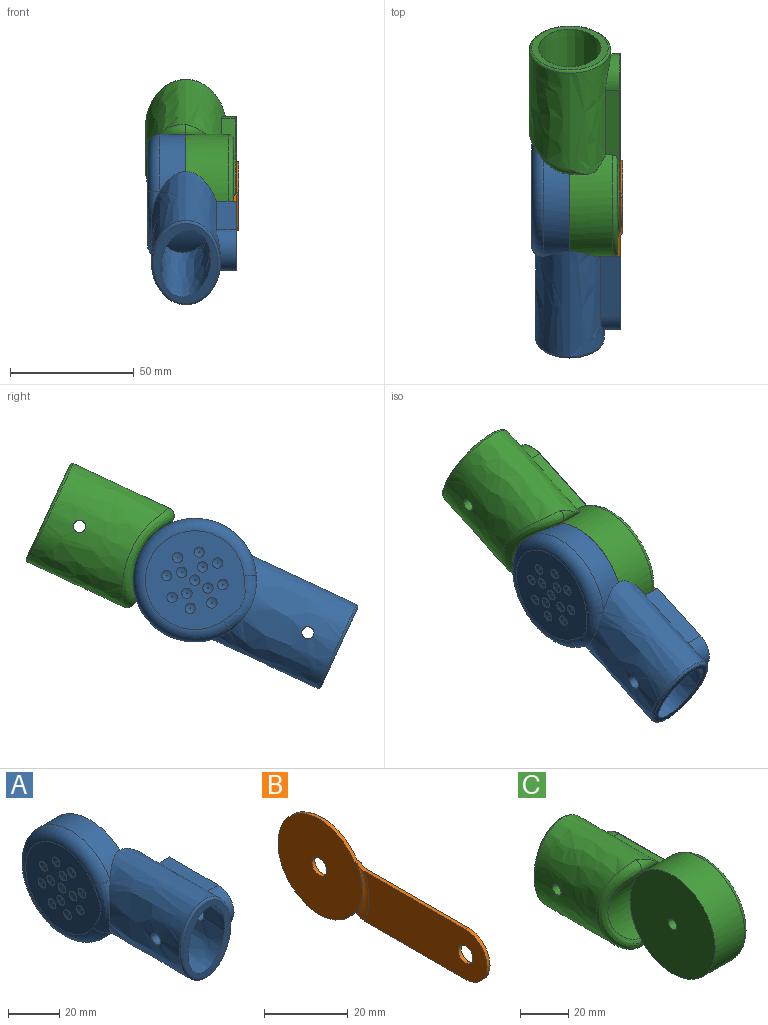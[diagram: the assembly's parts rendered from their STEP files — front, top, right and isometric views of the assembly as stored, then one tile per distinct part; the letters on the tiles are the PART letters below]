
ASSEMBLY  parts=3 mates=2
PART A: 53 faces, bbox 36x91.6x54.1 mm
  f0: cylinder r=2.5mm len=5mm, axis (1,0,0), area 58mm2, adj f1,f22
  f1: extruded ~46.96x37.5mm, area 3767.3mm2, adj f0,f2,f5,f7,f8,f9,f10,f11
  f2: cylinder r=25mm len=50mm, axis (1,0,0), area 1260.2mm2, adj f1,f4,f24
  f3: plane 41.43x40mm, normal (-1,0,0), area 1091.5mm2, adj f24,f25,f40,f41,f42,f43,f44,f45
  f4: plane 50x50mm, normal (1,0,0), area 1963.5mm2, adj f2,f5
  f5: cylinder r=25mm len=37.5mm, axis (1,0,0), area 450.2mm2, adj f1,f4
  f6: plane 35.51x26.01mm, normal (0,-1,0), area 252.8mm2, adj f22,f26
  f7: plane 26.98x8.07mm, normal (0,0,1), area 217.7mm2, adj f1,f8,f14,f15
  f8: cylinder r=8.75mm len=17.5mm, axis (1,0,0), area 199.2mm2, adj f1,f7,f9,f15
  f9: plane 26.96x8.07mm, normal (0,0,-1), area 217.5mm2, adj f1,f8,f10,f15
  f10: plane 8.07x1.26mm, normal (0,0.95,0.32), area 10.3mm2, adj f1,f9,f11,f15
  f11: plane 26.55x7.62mm, normal (0,0,1), area 202.3mm2, adj f1,f10,f12,f15
  f12: cylinder r=7.5mm len=15mm, axis (1,0,0), area 165.6mm2, adj f1,f11,f13,f15
  f13: plane 26.55x7.62mm, normal (0,0,-1), area 202.3mm2, adj f1,f12,f14,f15
  f14: plane 8.07x1.26mm, normal (0,0.94,-0.33), area 10.4mm2, adj f1,f7,f13,f15
  f15: plane 35.73x17.5mm, normal (1,0,0), area 98.8mm2, adj f7,f8,f9,f10,f11,f12,f13,f14
  f16: cylinder r=7.4mm len=14.8mm, axis (1,0,0), area 135.1mm2, adj f1,f17,f19,f20
  f17: plane 26.55x6.39mm, normal (0,0,-1), area 169.5mm2, adj f1,f16,f18,f20
  f18: extruded ~14.8x6.39mm, area 84.6mm2, adj f1,f17,f19,f20
  f19: plane 26.59x6.39mm, normal (0,0,1), area 169.8mm2, adj f1,f16,f18,f20
  f20: plane 33.99x14.8mm, normal (1,0,0), area 448.3mm2, adj f16,f17,f18,f19,f21
  f21: cylinder r=2.5mm len=9.55mm, axis (1,0,0), area 150mm2, adj f20,f22
  f22: extruded ~42.41x29.66mm, area 3105.8mm2, adj f0,f6,f21,f23
  f23: cylinder r=25mm len=29.75mm, axis (1,0,0), area 495.6mm2, adj f22
  f24: torus R=20mm, axis (1,0,0), area 955mm2, adj f2,f3,f25
  f25: bspline ~26.99x8.34mm, area 129mm2, adj f1,f3,f24
  f26: bspline ~37.52x28.01mm, area 158.9mm2, adj f1,f6
  f27: plane 0.28x0.28mm, normal (-1,0,0), area 0.1mm2, adj f52
  f28: plane 0.28x0.28mm, normal (-1,0,0), area 0.1mm2, adj f40
  f29: plane 0.28x0.28mm, normal (-1,0,0), area 0.1mm2, adj f41
  f30: plane 0.28x0.28mm, normal (-1,0,0), area 0.1mm2, adj f42
  f31: plane 0.28x0.28mm, normal (-1,0,0), area 0.1mm2, adj f43
  f32: plane 0.28x0.28mm, normal (-1,0,0), area 0.1mm2, adj f44
  f33: plane 0.28x0.28mm, normal (-1,0,0), area 0.1mm2, adj f45
  f34: plane 0.28x0.28mm, normal (-1,0,0), area 0.1mm2, adj f46
  f35: plane 0.28x0.28mm, normal (-1,0,0), area 0.1mm2, adj f47
  f36: plane 0.28x0.28mm, normal (-1,0,0), area 0.1mm2, adj f51
  f37: plane 0.28x0.28mm, normal (-1,0,0), area 0.1mm2, adj f50
  f38: plane 0.28x0.28mm, normal (-1,0,0), area 0.1mm2, adj f49
  f39: plane 0.28x0.28mm, normal (-1,0,0), area 0.1mm2, adj f48
  f40: torus R=0.14mm, axis (1,0,0), area 14.3mm2, adj f3,f28
  f41: torus R=0.14mm, axis (1,0,0), area 14.3mm2, adj f3,f29
  f42: torus R=0.14mm, axis (1,0,0), area 14.3mm2, adj f3,f30
  f43: torus R=0.14mm, axis (1,0,0), area 14.3mm2, adj f3,f31
  f44: torus R=0.14mm, axis (1,0,0), area 14.3mm2, adj f3,f32
  f45: torus R=0.14mm, axis (1,0,0), area 14.3mm2, adj f3,f33
  f46: torus R=0.14mm, axis (1,0,0), area 14.3mm2, adj f3,f34
  f47: torus R=0.14mm, axis (1,0,0), area 14.3mm2, adj f3,f35
  f48: torus R=0.14mm, axis (1,0,0), area 14.3mm2, adj f3,f39
  f49: torus R=0.14mm, axis (1,0,0), area 14.3mm2, adj f3,f38
  f50: torus R=0.14mm, axis (1,0,0), area 14.3mm2, adj f3,f37
  f51: torus R=0.14mm, axis (1,0,0), area 14.3mm2, adj f3,f36
  f52: torus R=0.14mm, axis (1,0,0), area 14.3mm2, adj f3,f27
PART B: 17 faces, bbox 2.1x71.9x28 mm
  f0: plane 27.9x26.91mm, normal (1,0,0), area 587.9mm2, adj f1,f2,f3,f4,f5,f8,f16
  f1: plane 38.63x2.07mm, normal (0,0,-1), area 38.8mm2, adj f0,f2,f7,f9,f10,f11,f12,f13
  f2: cylinder r=14mm len=26.54mm, axis (-1,0,0), area 51.8mm2, adj f0,f1,f3,f10
  f3: plane 1.45x1mm, normal (0,0.33,0.94), area 1.5mm2, adj f0,f2,f4,f10
  f4: cylinder r=13.9mm len=16.6mm, axis (-1,0,0), area 19mm2, adj f0,f3,f5,f10
  f5: plane 38.74x2.07mm, normal (0,0,1), area 38.9mm2, adj f0,f4,f7,f9,f10,f11,f12,f13
  f6: cylinder r=2.5mm len=5mm, axis (-1,0,0), area 15.7mm2, adj f9,f14
  f7: cylinder r=7.3mm len=14.6mm, axis (-1,0,0), area 22.9mm2, adj f1,f5,f9,f14
  f8: cylinder r=2.5mm len=5mm, axis (-1,0,0), area 15.7mm2, adj f0,f10
  f9: plane 41.55x14.6mm, normal (-1,0,0), area 548.7mm2, adj f1,f5,f6,f7,f12
  f10: plane 28.5x27.9mm, normal (-1,0,0), area 601.8mm2, adj f1,f2,f3,f4,f5,f8,f11
  f11: torus R=14.5mm, axis (1,0,0), area 9mm2, adj f1,f5,f10,f12
  f12: torus R=17.82mm, axis (1,0,0), area 44.5mm2, adj f1,f5,f9,f11
  f13: extruded ~14.6x2.59mm, area 39.6mm2, adj f1,f5,f14,f15
  f14: plane 41.55x14.6mm, normal (1,0,0), area 564.1mm2, adj f1,f5,f6,f7,f13
  f15: plane 14.6x0.21mm, normal (0.83,-0.55,0), area 3.6mm2, adj f1,f5,f13,f16
  f16: cylinder r=1mm len=14.6mm, axis (0,0,1), area 8.5mm2, adj f0,f1,f5,f15
PART C: 59 faces, bbox 37.4x93x54.6 mm
  f0: plane 50x50mm, normal (-1,0,0), area 1943.9mm2, adj f6,f9,f37
  f1: plane 42.01x31.01mm, normal (0,1,0), area 307.6mm2, adj f34,f57
  f2: plane 74.5x28mm, normal (1,0,0), area 17.6mm2, adj f3,f4,f5,f12,f13,f18,f20,f21
  f3: plane 32.42x0.65mm, normal (0,0,-1), area 21.1mm2, adj f2,f5,f12,f38
  f4: plane 32.42x0.65mm, normal (0,0,1), area 21.1mm2, adj f2,f5,f13,f41
  f5: cylinder r=9mm len=18mm, axis (1,0,0), area 18.4mm2, adj f2,f3,f4,f39
  f6: cylinder r=25mm len=50mm, axis (-1,0,0), area 2167.6mm2, adj f0,f8,f10,f11,f55,f56,f58
  f7: plane 46x43.46mm, normal (1,0,0), area 721.9mm2, adj f10,f11,f14,f15,f16,f17,f22,f58
  f8: extruded ~46.32x44mm, area 4219.3mm2, adj f6,f10,f11,f23,f36,f54,f55,f56
  f9: cylinder r=25mm len=32.46mm, axis (-1,0,0), area 351.4mm2, adj f0,f54
  f10: plane 32.85x5.88mm, normal (0,0,-1), area 160.3mm2, adj f6,f7,f8,f17,f23,f49,f58
  f11: plane 32.85x5.88mm, normal (0,0,1), area 160.3mm2, adj f6,f7,f8,f22,f23,f53,f58
  f12: cylinder r=15mm len=5.02mm, axis (1,0,0), area 3.3mm2, adj f2,f3,f20,f40
  f13: cylinder r=15mm len=5.02mm, axis (1,0,0), area 3.3mm2, adj f2,f4,f18,f43
  f14: plane 9.25x3.28mm, normal (0,0.33,0.94), area 6.4mm2, adj f7,f15,f22,f50
  f15: cylinder r=15.5mm len=31mm, axis (1,0,0), area 38.7mm2, adj f7,f14,f16,f48
  f16: plane 9.25x3.28mm, normal (0,0.33,-0.94), area 6.4mm2, adj f7,f15,f17,f46
  f17: cylinder r=13.5mm len=4.51mm, axis (1,0,0), area 3mm2, adj f7,f10,f16,f47
  f18: plane 9.26x3.28mm, normal (0,-0.33,0.94), area 6.4mm2, adj f2,f13,f21,f45
  f19: plane 76.5x30mm, normal (1,0,0), area 90.7mm2, adj f38,f39,f40,f41,f42,f43,f44,f45
  f20: plane 9.26x3.28mm, normal (0,-0.33,-0.94), area 6.4mm2, adj f2,f12,f21,f42
  f21: cylinder r=14mm len=28mm, axis (1,0,0), area 35mm2, adj f2,f18,f20,f44
  f22: cylinder r=13.5mm len=4.51mm, axis (1,0,0), area 3mm2, adj f7,f11,f14,f52
  f23: cylinder r=10.5mm len=21mm, axis (1,0,0), area 146.3mm2, adj f8,f10,f11,f51
  f24: plane 74.3x27.8mm, normal (1,0,0), area 1399.8mm2, adj f25,f26,f27,f28,f29,f30,f31,f32
  f25: plane 32.42x1.15mm, normal (0,0,-1), area 37.3mm2, adj f2,f24,f26,f32
  f26: cylinder r=8.9mm len=17.8mm, axis (-1,0,0), area 32.2mm2, adj f2,f24,f25,f27
  f27: plane 32.42x1.15mm, normal (0,0,1), area 37.3mm2, adj f2,f24,f26,f28
  f28: cylinder r=15.1mm len=5.05mm, axis (-1,0,0), area 5.9mm2, adj f2,f24,f27,f29
  f29: plane 9.26x3.29mm, normal (0,0.33,0.94), area 11.3mm2, adj f2,f24,f28,f30
  f30: cylinder r=13.9mm len=27.8mm, axis (-1,0,0), area 61.4mm2, adj f2,f24,f29,f31
  f31: plane 9.26x3.29mm, normal (0,0.33,-0.94), area 11.3mm2, adj f2,f24,f30,f32
  f32: cylinder r=15.1mm len=5.05mm, axis (-1,0,0), area 5.9mm2, adj f2,f24,f25,f31
  f33: cylinder r=25mm len=36.2mm, axis (-1,0,0), area 774.2mm2, adj f34
  f34: extruded ~47.26x36.2mm, area 4111.8mm2, adj f1,f33,f35,f36
  f35: cylinder r=2.5mm len=7.97mm, axis (1,0,0), area 125.2mm2, adj f24,f34
  f36: cylinder r=2.5mm len=5mm, axis (1,0,0), area 61.5mm2, adj f8,f34
  f37: cylinder r=2.5mm len=20.45mm, axis (1,0,0), area 321.2mm2, adj f0,f24
  f38: cylinder r=0.5mm len=32.42mm, axis (0,1,0), area 25.5mm2, adj f3,f19,f39,f40
  f39: torus R=9.5mm, axis (1,0,0), area 22.7mm2, adj f5,f19,f38,f41
  f40: torus R=14.5mm, axis (1,0,0), area 4mm2, adj f12,f19,f38,f42
  f41: cylinder r=0.5mm len=32.42mm, axis (0,-1,0), area 25.5mm2, adj f4,f19,f39,f43
  f42: cylinder r=0.5mm len=9.43mm, axis (0,0.94,-0.33), area 7.7mm2, adj f19,f20,f40,f44
  f43: torus R=14.5mm, axis (1,0,0), area 4mm2, adj f13,f19,f41,f45
  f44: torus R=14.5mm, axis (1,0,0), area 42.8mm2, adj f19,f21,f42,f45
  f45: cylinder r=0.5mm len=9.43mm, axis (0,-0.94,-0.33), area 7.7mm2, adj f18,f19,f43,f44
  f46: cylinder r=0.5mm len=9.42mm, axis (0,0.94,0.33), area 7.7mm2, adj f16,f19,f47,f48
  f47: torus R=14mm, axis (1,0,0), area 3.7mm2, adj f17,f19,f46,f49
  f48: torus R=15mm, axis (1,0,0), area 46.2mm2, adj f15,f19,f46,f50
  f49: cylinder r=0.5mm len=32.42mm, axis (0,1,0), area 25.5mm2, adj f10,f19,f47,f51
  f50: cylinder r=0.5mm len=9.42mm, axis (0,-0.94,0.33), area 7.7mm2, adj f14,f19,f48,f52
  f51: torus R=10mm, axis (1,0,0), area 25.5mm2, adj f19,f23,f49,f53
  f52: torus R=14mm, axis (1,0,0), area 3.7mm2, adj f19,f22,f50,f53
  f53: cylinder r=0.5mm len=32.42mm, axis (0,-1,0), area 25.5mm2, adj f11,f19,f51,f52
  f54: bspline ~44.03x18.37mm, area 375.6mm2, adj f8,f9,f55,f56
  f55: cylinder r=3.5mm len=11.14mm, axis (-1,0,0), area 51.5mm2, adj f6,f8,f54
  f56: cylinder r=3.5mm len=11.14mm, axis (-1,0,0), area 51.5mm2, adj f6,f8,f54
  f57: bspline ~44.02x33.01mm, area 187.3mm2, adj f1,f8
  f58: torus R=23mm, axis (1,0,0), area 410mm2, adj f6,f7,f10,f11
PLACE A rot(axis=(1,0,0),25deg) t=(-35.84,58.28,-29.16)mm fixed
PLACE B rot(axis=(1,0,0),25deg) t=(-35.84,58.28,-29.16)mm
PLACE C rot(axis=(1,0,0),25deg) t=(-35.84,58.28,-29.16)mm
MATE fastened B.f6 <-> A.f0  axis (-1,0,0) through (-16.39,12.51,-50.5)mm
MATE revolute A.f2 <-> C.f37  axis (1,0,0) through (-35.84,58.28,-29.16)mm
